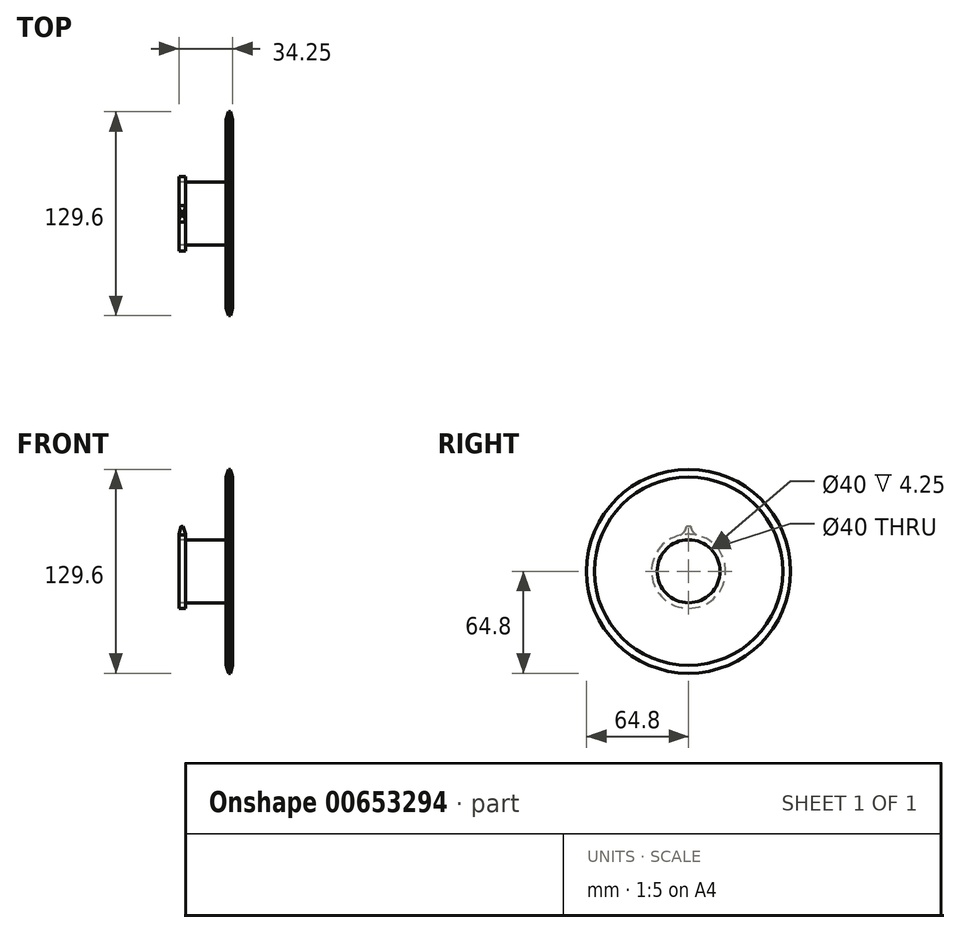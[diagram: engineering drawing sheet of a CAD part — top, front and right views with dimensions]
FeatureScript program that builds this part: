
annotation { "Feature Type Name" : "Feature", "Feature Type Description" : "" }
export const myFeature = defineFeature(function(context is Context, id is Id, definition is map)
    precondition{}
    {
        {
            var Q0;
            Q0=qCreatedBy(makeId("Front.planeOp"),FACE);
            var sketch = newSketch(context, id + "F0", { "sketchPlane" : qUnion([Q0])});
            skLineSegment(sketch, "E0", {"start": v(0, 20) * mm, "end": v(4.25, 20) * mm});
            skLineSegment(sketch, "E1", {"start": v(4.25, 20) * mm, "end": v(4.25, 28.55) * mm});
            skLineSegment(sketch, "E2", {"start": v(4.25, 28.55) * mm, "end": v(0, 28.55) * mm});
            skLineSegment(sketch, "E3", {"start": v(0, 28.55) * mm, "end": v(0, 20) * mm});
            skLineSegment(sketch, "E4", {"start": v(0, 0) * mm, "end": v(23.45, 0) * mm, "construction": true});
            skSolve(sketch);
        }
        {
            var Q0;
            Q0=makeQuery(id+"F0.imprint","IMPRINT",FACE,{"disambiguationData":[TD([[makeQuery(id+"F0.imprint","IMPRINT",EDGE,{"derivedFrom":sQuery(id+"F0.wireOp",EDGE,"E0")}),1.0]])]});
            var Q1;
            Q1=sQuery(id+"F0.wireOp",EDGE,"E4");
            revolve(context, id + "F1", {"entities" : qUnion([Q0]), "axis" : qUnion([Q1]), "revolveType" : RevolveType.FULL});
        }
        {
            var Q0;
            Q0=makeQuery(id+"F1.opRevolve","SWEPT_EDGE",EDGE,{"disambiguationData":[OSD([sQuery(id+"F0.wireOp",EDGE,"E1"),sQuery(id+"F0.wireOp",EDGE,"E2")])]});
            var Q1;
            Q1=makeQuery(id+"F1.opRevolve","SWEPT_EDGE",EDGE,{"disambiguationData":[OSD([sQuery(id+"F0.wireOp",EDGE,"E2"),sQuery(id+"F0.wireOp",EDGE,"E3")])]});
            chamfer(context, id + "F2", {"entities" : qUnion([Q0, Q1]), "chamferType" : ChamferType.TWO_OFFSETS, "width1" : 1.5 * mm, "oppositeDirection" : false, "width2" : 5 * mm});
        }
        {
            var Q0;
            Q0=makeQuery(id+"F1.opRevolve","SWEPT_FACE",FACE,{"disambiguationData":[OSD([sQuery(id+"F0.wireOp",EDGE,"E3")])]});
            var sketch = newSketch(context, id + "F3", { "sketchPlane" : qUnion([Q0])});
            skCircle(sketch, "E5.1", {"center": v(0, 0) * mm, "radius": 20 * mm});
            skLineSegment(sketch, "E6", {"start": v(0, 29.71) * mm, "end": v(-0.16, 29.47) * mm});
            skLineSegment(sketch, "E7", {"start": v(0, 29.71) * mm, "end": v(0.16, 29.47) * mm});
            skLineSegment(sketch, "E8", {"start": v(0, 0) * mm, "end": v(0, 29.47) * mm, "construction": true});
            skArc(sketch, "E9", {"start": v(-0.02, 29.47) * mm, "mid": v(0, 29.59) * mm, "end": v(0, 29.71) * mm});
            skArc(sketch, "E10.MirrorCS", {"start": v(0.02, 29.47) * mm, "mid": v(0, 29.59) * mm, "end": v(0, 29.71) * mm});
            skLineSegment(sketch, "E11", {"start": v(1.3, 29.47) * mm, "end": v(-1.3, 29.47) * mm});
            skArc(sketch, "E12", {"start": v(1.3, 29.47) * mm, "mid": v(2.4, 25.74) * mm, "end": v(5.14, 22.98) * mm});
            skArc(sketch, "E13.MirrorCS", {"start": v(-1.3, 29.47) * mm, "mid": v(-2.4, 25.74) * mm, "end": v(-5.14, 22.98) * mm});
            skPoint(sketch, "E14.orphan", {"position": v(4.22, 23.17) * mm});
            skLineSegment(sketch, "E15.trimOffspring", {"start": v(-0.16, 29.47) * mm, "end": v(0, 29.71) * mm});
            skPoint(sketch, "E16.trimOffspring.end.orphan", {"position": v(-4.22, 23.17) * mm});
            skArc(sketch, "E17.1.0", {"start": v(-13.96, 25.99) * mm, "mid": v(-13.32, 22.15) * mm, "end": v(-14.6, 18.47) * mm});
            skLineSegment(sketch, "E17.1.1", {"start": v(-11.62, 27.11) * mm, "end": v(-13.96, 25.99) * mm});
            skArc(sketch, "E17.1.2", {"start": v(-11.62, 27.11) * mm, "mid": v(-9, 24.23) * mm, "end": v(-5.34, 22.94) * mm});
            skArc(sketch, "E17.2.0", {"start": v(-23.85, 17.36) * mm, "mid": v(-21.61, 14.17) * mm, "end": v(-21.17, 10.3) * mm});
            skLineSegment(sketch, "E17.2.1", {"start": v(-22.23, 19.39) * mm, "end": v(-23.85, 17.36) * mm});
            skArc(sketch, "E17.2.2", {"start": v(-22.23, 19.39) * mm, "mid": v(-18.63, 17.92) * mm, "end": v(-14.76, 18.35) * mm});
            skArc(sketch, "E17.3.0", {"start": v(-29.02, 5.3) * mm, "mid": v(-25.62, 3.4) * mm, "end": v(-23.55, 0.1) * mm});
            skLineSegment(sketch, "E17.3.1", {"start": v(-28.44, 7.82) * mm, "end": v(-29.02, 5.3) * mm});
            skArc(sketch, "E17.3.2", {"start": v(-28.44, 7.82) * mm, "mid": v(-24.56, 8.06) * mm, "end": v(-21.26, 10.13) * mm});
            skArc(sketch, "E17.4.0", {"start": v(-28.44, -7.82) * mm, "mid": v(-24.56, -8.06) * mm, "end": v(-21.26, -10.13) * mm});
            skLineSegment(sketch, "E17.4.1", {"start": v(-29.02, -5.3) * mm, "end": v(-28.44, -7.82) * mm});
            skArc(sketch, "E17.4.2", {"start": v(-29.02, -5.3) * mm, "mid": v(-25.62, -3.4) * mm, "end": v(-23.55, -0.1) * mm});
            skArc(sketch, "E17.5.0", {"start": v(-22.23, -19.39) * mm, "mid": v(-18.63, -17.92) * mm, "end": v(-14.76, -18.35) * mm});
            skLineSegment(sketch, "E17.5.1", {"start": v(-23.85, -17.36) * mm, "end": v(-22.23, -19.39) * mm});
            skArc(sketch, "E17.5.2", {"start": v(-23.85, -17.36) * mm, "mid": v(-21.61, -14.17) * mm, "end": v(-21.17, -10.3) * mm});
            skArc(sketch, "E17.6.0", {"start": v(-11.62, -27.11) * mm, "mid": v(-9, -24.23) * mm, "end": v(-5.34, -22.94) * mm});
            skLineSegment(sketch, "E17.6.1", {"start": v(-13.96, -25.99) * mm, "end": v(-11.62, -27.11) * mm});
            skArc(sketch, "E17.6.2", {"start": v(-13.96, -25.99) * mm, "mid": v(-13.32, -22.15) * mm, "end": v(-14.6, -18.47) * mm});
            skArc(sketch, "E17.7.0", {"start": v(1.3, -29.47) * mm, "mid": v(2.4, -25.74) * mm, "end": v(5.14, -22.98) * mm});
            skLineSegment(sketch, "E17.7.1", {"start": v(-1.3, -29.47) * mm, "end": v(1.3, -29.47) * mm});
            skArc(sketch, "E17.7.2", {"start": v(-1.3, -29.47) * mm, "mid": v(-2.4, -25.74) * mm, "end": v(-5.14, -22.98) * mm});
            skArc(sketch, "E17.8.0", {"start": v(13.96, -25.99) * mm, "mid": v(13.32, -22.15) * mm, "end": v(14.6, -18.47) * mm});
            skLineSegment(sketch, "E17.8.1", {"start": v(11.62, -27.11) * mm, "end": v(13.96, -25.99) * mm});
            skArc(sketch, "E17.8.2", {"start": v(11.62, -27.11) * mm, "mid": v(9, -24.23) * mm, "end": v(5.34, -22.94) * mm});
            skArc(sketch, "E17.9.0", {"start": v(23.85, -17.36) * mm, "mid": v(21.61, -14.17) * mm, "end": v(21.17, -10.3) * mm});
            skLineSegment(sketch, "E17.9.1", {"start": v(22.23, -19.39) * mm, "end": v(23.85, -17.36) * mm});
            skArc(sketch, "E17.9.2", {"start": v(22.23, -19.39) * mm, "mid": v(18.63, -17.92) * mm, "end": v(14.76, -18.35) * mm});
            skArc(sketch, "E17.10.0", {"start": v(29.02, -5.3) * mm, "mid": v(25.62, -3.4) * mm, "end": v(23.55, -0.1) * mm});
            skLineSegment(sketch, "E17.10.1", {"start": v(28.44, -7.82) * mm, "end": v(29.02, -5.3) * mm});
            skArc(sketch, "E17.10.2", {"start": v(28.44, -7.82) * mm, "mid": v(24.56, -8.06) * mm, "end": v(21.26, -10.13) * mm});
            skArc(sketch, "E17.11.0", {"start": v(28.44, 7.82) * mm, "mid": v(24.56, 8.06) * mm, "end": v(21.26, 10.13) * mm});
            skLineSegment(sketch, "E17.11.1", {"start": v(29.02, 5.3) * mm, "end": v(28.44, 7.82) * mm});
            skArc(sketch, "E17.11.2", {"start": v(29.02, 5.3) * mm, "mid": v(25.62, 3.4) * mm, "end": v(23.55, 0.1) * mm});
            skArc(sketch, "E17.12.0", {"start": v(22.23, 19.39) * mm, "mid": v(18.63, 17.92) * mm, "end": v(14.76, 18.35) * mm});
            skLineSegment(sketch, "E17.12.1", {"start": v(23.85, 17.36) * mm, "end": v(22.23, 19.39) * mm});
            skArc(sketch, "E17.12.2", {"start": v(23.85, 17.36) * mm, "mid": v(21.61, 14.17) * mm, "end": v(21.17, 10.3) * mm});
            skArc(sketch, "E17.13.0", {"start": v(11.62, 27.11) * mm, "mid": v(9, 24.23) * mm, "end": v(5.34, 22.94) * mm});
            skLineSegment(sketch, "E17.13.1", {"start": v(13.96, 25.99) * mm, "end": v(11.62, 27.11) * mm});
            skArc(sketch, "E17.13.2", {"start": v(13.96, 25.99) * mm, "mid": v(13.32, 22.15) * mm, "end": v(14.6, 18.47) * mm});
            skSolve(sketch);
        }
        {
            var Q0;
            {var subQ5=sQuery(id+"F3.wireOp",EDGE,"E12");Q0=makeQuery(id+"F3.imprint","IMPRINT",FACE,{"disambiguationData":[TD([[makeQuery(id+"F3.imprint","IMPRINT",EDGE,{"derivedFrom":subQ5}),-1.0]])]});}
            var Q1;
            Q1=makeQuery(id+"F3.imprint","IMPRINT",FACE,{"disambiguationData":[TD([[makeQuery(id+"F3.imprint","IMPRINT",EDGE,{"derivedFrom":sQuery(id+"F3.wireOp",EDGE,"E5.1")}),-1.0]])]});
            var Q2;
            {var subQ0=sQuery(id+"F3.wireOp",EDGE,"E17.13.0");Q2=makeQuery(id+"F3.imprint","IMPRINT",FACE,{"disambiguationData":[TD([[makeQuery(id+"F3.imprint","IMPRINT",EDGE,{"derivedFrom":subQ0}),1.0]])]});}
            var Q3;
            {var subQ0=sQuery(id+"F3.wireOp",EDGE,"E17.12.0");Q3=makeQuery(id+"F3.imprint","IMPRINT",FACE,{"disambiguationData":[TD([[makeQuery(id+"F3.imprint","IMPRINT",EDGE,{"derivedFrom":subQ0}),1.0]])]});}
            var Q4;
            {var subQ0=sQuery(id+"F3.wireOp",EDGE,"E17.11.0");Q4=makeQuery(id+"F3.imprint","IMPRINT",FACE,{"disambiguationData":[TD([[makeQuery(id+"F3.imprint","IMPRINT",EDGE,{"derivedFrom":subQ0}),1.0]])]});}
            var Q5;
            {var subQ0=sQuery(id+"F3.wireOp",EDGE,"E17.10.0");Q5=makeQuery(id+"F3.imprint","IMPRINT",FACE,{"disambiguationData":[TD([[makeQuery(id+"F3.imprint","IMPRINT",EDGE,{"derivedFrom":subQ0}),1.0]])]});}
            var Q6;
            {var subQ0=sQuery(id+"F3.wireOp",EDGE,"E17.9.0");Q6=makeQuery(id+"F3.imprint","IMPRINT",FACE,{"disambiguationData":[TD([[makeQuery(id+"F3.imprint","IMPRINT",EDGE,{"derivedFrom":subQ0}),1.0]])]});}
            var Q7;
            {var subQ0=sQuery(id+"F3.wireOp",EDGE,"E17.8.0");Q7=makeQuery(id+"F3.imprint","IMPRINT",FACE,{"disambiguationData":[TD([[makeQuery(id+"F3.imprint","IMPRINT",EDGE,{"derivedFrom":subQ0}),1.0]])]});}
            var Q8;
            {var subQ0=sQuery(id+"F3.wireOp",EDGE,"E17.7.0");Q8=makeQuery(id+"F3.imprint","IMPRINT",FACE,{"disambiguationData":[TD([[makeQuery(id+"F3.imprint","IMPRINT",EDGE,{"derivedFrom":subQ0}),1.0]])]});}
            var Q9;
            {var subQ0=sQuery(id+"F3.wireOp",EDGE,"E17.6.0");Q9=makeQuery(id+"F3.imprint","IMPRINT",FACE,{"disambiguationData":[TD([[makeQuery(id+"F3.imprint","IMPRINT",EDGE,{"derivedFrom":subQ0}),1.0]])]});}
            var Q10;
            {var subQ0=sQuery(id+"F3.wireOp",EDGE,"E17.5.0");Q10=makeQuery(id+"F3.imprint","IMPRINT",FACE,{"disambiguationData":[TD([[makeQuery(id+"F3.imprint","IMPRINT",EDGE,{"derivedFrom":subQ0}),1.0]])]});}
            var Q11;
            {var subQ0=sQuery(id+"F3.wireOp",EDGE,"E17.4.0");Q11=makeQuery(id+"F3.imprint","IMPRINT",FACE,{"disambiguationData":[TD([[makeQuery(id+"F3.imprint","IMPRINT",EDGE,{"derivedFrom":subQ0}),1.0]])]});}
            var Q12;
            {var subQ0=sQuery(id+"F3.wireOp",EDGE,"E17.3.0");Q12=makeQuery(id+"F3.imprint","IMPRINT",FACE,{"disambiguationData":[TD([[makeQuery(id+"F3.imprint","IMPRINT",EDGE,{"derivedFrom":subQ0}),1.0]])]});}
            var Q13;
            {var subQ0=sQuery(id+"F3.wireOp",EDGE,"E17.2.0");Q13=makeQuery(id+"F3.imprint","IMPRINT",FACE,{"disambiguationData":[TD([[makeQuery(id+"F3.imprint","IMPRINT",EDGE,{"derivedFrom":subQ0}),1.0]])]});}
            var Q14;
            {var subQ0=sQuery(id+"F3.wireOp",EDGE,"E17.1.0");Q14=makeQuery(id+"F3.imprint","IMPRINT",FACE,{"disambiguationData":[TD([[makeQuery(id+"F3.imprint","IMPRINT",EDGE,{"derivedFrom":subQ0}),1.0]])]});}
            extrude(context, id + "F4", {"entities" : qUnion([Q0, Q1, Q2, Q3, Q4, Q5, Q6, Q7, Q8, Q9, Q10, Q11, Q12, Q13, Q14]), "operationType" : NewBodyOperationType.INTERSECT, "oppositeDirection" : true, "depth" : 25 * mm, "offsetDistance" : 25 * mm});
        }
        {
            var Q0;
            Q0=qCreatedBy(makeId("Front.planeOp"),FACE);
            var sketch = newSketch(context, id + "F5", { "sketchPlane" : qUnion([Q0])});
            skPoint(sketch, "E18.0", {"position": v(2.13, 0.1) * mm});
            skLineSegment(sketch, "E19", {"start": v(2.13, 0) * mm, "end": v(32.12, 0) * mm, "construction": true});
            skLineSegment(sketch, "E20", {"start": v(30, 20) * mm, "end": v(34.25, 20) * mm});
            skLineSegment(sketch, "E21", {"start": v(34.25, 20) * mm, "end": v(34.25, 64.8) * mm});
            skLineSegment(sketch, "E22", {"start": v(34.25, 64.8) * mm, "end": v(30, 64.8) * mm});
            skLineSegment(sketch, "E23", {"start": v(30, 64.8) * mm, "end": v(30, 20) * mm});
            skLineSegment(sketch, "E24", {"start": v(30, 0) * mm, "end": v(53.45, 0) * mm, "construction": true});
            skSolve(sketch);
        }
        {
            var Q0;
            Q0=makeQuery(id+"F5.imprint","IMPRINT",FACE,{"disambiguationData":[TD([[makeQuery(id+"F5.imprint","IMPRINT",EDGE,{"derivedFrom":sQuery(id+"F5.wireOp",EDGE,"E20")}),1.0]])]});
            var Q1;
            Q1=sQuery(id+"F5.wireOp",EDGE,"E24");
            revolve(context, id + "F6", {"entities" : qUnion([Q0]), "axis" : qUnion([Q1]), "revolveType" : RevolveType.FULL});
        }
        {
            var Q0;
            Q0=makeQuery(id+"F6.opRevolve","SWEPT_EDGE",EDGE,{"disambiguationData":[OSD([sQuery(id+"F5.wireOp",EDGE,"E21"),sQuery(id+"F5.wireOp",EDGE,"E22")])]});
            var Q1;
            Q1=makeQuery(id+"F6.opRevolve","SWEPT_EDGE",EDGE,{"disambiguationData":[OSD([sQuery(id+"F5.wireOp",EDGE,"E22"),sQuery(id+"F5.wireOp",EDGE,"E23")])]});
            chamfer(context, id + "F7", {"entities" : qUnion([Q0, Q1]), "chamferType" : ChamferType.TWO_OFFSETS, "width1" : 1.5 * mm, "oppositeDirection" : false, "width2" : 5 * mm, "tangentPropagation" : true});
        }
        {
            var Q0;
            Q0=makeQuery(id+"F6.opRevolve","SWEPT_FACE",FACE,{"disambiguationData":[OSD([sQuery(id+"F5.wireOp",EDGE,"E23")])]});
            var sketch = newSketch(context, id + "F8", { "sketchPlane" : qUnion([Q0])});
            skCircle(sketch, "E25.1", {"center": v(0, 0) * mm, "radius": 20 * mm});
            skLineSegment(sketch, "E26", {"start": v(0, 29.71) * mm, "end": v(-0.16, 29.47) * mm});
            skLineSegment(sketch, "E27", {"start": v(0, 29.71) * mm, "end": v(0.16, 29.47) * mm});
            skLineSegment(sketch, "E28", {"start": v(0, 0) * mm, "end": v(0, 29.47) * mm, "construction": true});
            skArc(sketch, "E29", {"start": v(-0.02, 29.47) * mm, "mid": v(0, 29.59) * mm, "end": v(0, 29.71) * mm});
            skArc(sketch, "E30.MirrorCS", {"start": v(0.02, 29.47) * mm, "mid": v(0, 29.59) * mm, "end": v(0, 29.71) * mm});
            skLineSegment(sketch, "E31", {"start": v(1.3, 29.47) * mm, "end": v(-1.3, 29.47) * mm});
            skArc(sketch, "E32", {"start": v(1.3, 29.47) * mm, "mid": v(2.4, 25.74) * mm, "end": v(5.14, 22.98) * mm});
            skArc(sketch, "E33.MirrorCS", {"start": v(-1.3, 29.47) * mm, "mid": v(-2.4, 25.74) * mm, "end": v(-5.14, 22.98) * mm});
            skPoint(sketch, "E34.orphan", {"position": v(4.22, 23.17) * mm});
            skLineSegment(sketch, "E35.trimOffspring", {"start": v(-0.16, 29.47) * mm, "end": v(0, 29.71) * mm});
            skPoint(sketch, "E36.trimOffspring.end.orphan", {"position": v(-4.22, 23.17) * mm});
            skArc(sketch, "E37.1.0", {"start": v(-13.96, 25.99) * mm, "mid": v(-13.32, 22.15) * mm, "end": v(-14.6, 18.47) * mm});
            skLineSegment(sketch, "E37.1.1", {"start": v(-11.62, 27.11) * mm, "end": v(-13.96, 25.99) * mm});
            skArc(sketch, "E37.1.2", {"start": v(-11.62, 27.11) * mm, "mid": v(-9, 24.23) * mm, "end": v(-5.34, 22.94) * mm});
            skArc(sketch, "E37.2.0", {"start": v(-23.85, 17.36) * mm, "mid": v(-21.61, 14.17) * mm, "end": v(-21.17, 10.3) * mm});
            skLineSegment(sketch, "E37.2.1", {"start": v(-22.23, 19.39) * mm, "end": v(-23.85, 17.36) * mm});
            skArc(sketch, "E37.2.2", {"start": v(-22.23, 19.39) * mm, "mid": v(-18.63, 17.92) * mm, "end": v(-14.76, 18.35) * mm});
            skArc(sketch, "E37.3.0", {"start": v(-29.02, 5.3) * mm, "mid": v(-25.62, 3.4) * mm, "end": v(-23.55, 0.1) * mm});
            skLineSegment(sketch, "E37.3.1", {"start": v(-28.44, 7.82) * mm, "end": v(-29.02, 5.3) * mm});
            skArc(sketch, "E37.3.2", {"start": v(-28.44, 7.82) * mm, "mid": v(-24.56, 8.06) * mm, "end": v(-21.26, 10.13) * mm});
            skArc(sketch, "E37.4.0", {"start": v(-28.44, -7.82) * mm, "mid": v(-24.56, -8.06) * mm, "end": v(-21.26, -10.13) * mm});
            skLineSegment(sketch, "E37.4.1", {"start": v(-29.02, -5.3) * mm, "end": v(-28.44, -7.82) * mm});
            skArc(sketch, "E37.4.2", {"start": v(-29.02, -5.3) * mm, "mid": v(-25.62, -3.4) * mm, "end": v(-23.55, -0.1) * mm});
            skArc(sketch, "E37.5.0", {"start": v(-22.23, -19.39) * mm, "mid": v(-18.63, -17.92) * mm, "end": v(-14.76, -18.35) * mm});
            skLineSegment(sketch, "E37.5.1", {"start": v(-23.85, -17.36) * mm, "end": v(-22.23, -19.39) * mm});
            skArc(sketch, "E37.5.2", {"start": v(-23.85, -17.36) * mm, "mid": v(-21.61, -14.17) * mm, "end": v(-21.17, -10.3) * mm});
            skArc(sketch, "E37.6.0", {"start": v(-11.62, -27.11) * mm, "mid": v(-9, -24.23) * mm, "end": v(-5.34, -22.94) * mm});
            skLineSegment(sketch, "E37.6.1", {"start": v(-13.96, -25.99) * mm, "end": v(-11.62, -27.11) * mm});
            skArc(sketch, "E37.6.2", {"start": v(-13.96, -25.99) * mm, "mid": v(-13.32, -22.15) * mm, "end": v(-14.6, -18.47) * mm});
            skArc(sketch, "E37.7.0", {"start": v(1.3, -29.47) * mm, "mid": v(2.4, -25.74) * mm, "end": v(5.14, -22.98) * mm});
            skLineSegment(sketch, "E37.7.1", {"start": v(-1.3, -29.47) * mm, "end": v(1.3, -29.47) * mm});
            skArc(sketch, "E37.7.2", {"start": v(-1.3, -29.47) * mm, "mid": v(-2.4, -25.74) * mm, "end": v(-5.14, -22.98) * mm});
            skArc(sketch, "E37.8.0", {"start": v(13.96, -25.99) * mm, "mid": v(13.32, -22.15) * mm, "end": v(14.6, -18.47) * mm});
            skLineSegment(sketch, "E37.8.1", {"start": v(11.62, -27.11) * mm, "end": v(13.96, -25.99) * mm});
            skArc(sketch, "E37.8.2", {"start": v(11.62, -27.11) * mm, "mid": v(9, -24.23) * mm, "end": v(5.34, -22.94) * mm});
            skArc(sketch, "E37.9.0", {"start": v(23.85, -17.36) * mm, "mid": v(21.61, -14.17) * mm, "end": v(21.17, -10.3) * mm});
            skLineSegment(sketch, "E37.9.1", {"start": v(22.23, -19.39) * mm, "end": v(23.85, -17.36) * mm});
            skArc(sketch, "E37.9.2", {"start": v(22.23, -19.39) * mm, "mid": v(18.63, -17.92) * mm, "end": v(14.76, -18.35) * mm});
            skArc(sketch, "E37.10.0", {"start": v(29.02, -5.3) * mm, "mid": v(25.62, -3.4) * mm, "end": v(23.55, -0.1) * mm});
            skLineSegment(sketch, "E37.10.1", {"start": v(28.44, -7.82) * mm, "end": v(29.02, -5.3) * mm});
            skArc(sketch, "E37.10.2", {"start": v(28.44, -7.82) * mm, "mid": v(24.56, -8.06) * mm, "end": v(21.26, -10.13) * mm});
            skArc(sketch, "E37.11.0", {"start": v(28.44, 7.82) * mm, "mid": v(24.56, 8.06) * mm, "end": v(21.26, 10.13) * mm});
            skLineSegment(sketch, "E37.11.1", {"start": v(29.02, 5.3) * mm, "end": v(28.44, 7.82) * mm});
            skArc(sketch, "E37.11.2", {"start": v(29.02, 5.3) * mm, "mid": v(25.62, 3.4) * mm, "end": v(23.55, 0.1) * mm});
            skArc(sketch, "E37.12.0", {"start": v(22.23, 19.39) * mm, "mid": v(18.63, 17.92) * mm, "end": v(14.76, 18.35) * mm});
            skLineSegment(sketch, "E37.12.1", {"start": v(23.85, 17.36) * mm, "end": v(22.23, 19.39) * mm});
            skArc(sketch, "E37.12.2", {"start": v(23.85, 17.36) * mm, "mid": v(21.61, 14.17) * mm, "end": v(21.17, 10.3) * mm});
            skArc(sketch, "E37.13.0", {"start": v(11.62, 27.11) * mm, "mid": v(9, 24.23) * mm, "end": v(5.34, 22.94) * mm});
            skLineSegment(sketch, "E37.13.1", {"start": v(13.96, 25.99) * mm, "end": v(11.62, 27.11) * mm});
            skArc(sketch, "E37.13.2", {"start": v(13.96, 25.99) * mm, "mid": v(13.32, 22.15) * mm, "end": v(14.6, 18.47) * mm});
            skSolve(sketch);
        }
        {
            var Q0;
            Q0=makeQuery(id+"F8.imprint","IMPRINT",FACE,{"disambiguationData":[TD([[makeQuery(id+"F8.imprint","IMPRINT",EDGE,{"derivedFrom":sQuery(id+"F8.wireOp",EDGE,"E25.1")}),-1.0]])]});
            var sketch = newSketch(context, id + "F9", { "sketchPlane" : qUnion([Q0])});
            skCircle(sketch, "E38.0", {"center": v(0, 0) * mm, "radius": 20 * mm});
            skSolve(sketch);
        }
        {
            var Q0;
            Q0 = qSketchRegion(id + "F9", true);
            var Q1;
            Q1=makeQuery(id+"F3.imprint","IMPRINT",FACE,{"disambiguationData":[TD([[makeQuery(id+"F3.imprint","IMPRINT",EDGE,{"derivedFrom":sQuery(id+"F3.wireOp",EDGE,"E5.1")}),1.0]])]});
            var Q2;
            Q2=makeQuery(id+"F6.opRevolve","SWEPT_FACE",FACE,{"disambiguationData":[OSD([sQuery(id+"F5.wireOp",EDGE,"E21")])]});
            extrude(context, id + "F10", {"entities" : qUnion([Q0, Q1]), "endBound" : BoundingType.UP_TO_SURFACE, "oppositeDirection" : true, "depth" : 25 * mm, "endBoundEntityFace" : qUnion([Q2]), "offsetDistance" : 25 * mm});
        }
        {
            var Q0;
            Q0=makeQuery(id+"F10.opExtrude","SWEPT_BODY",BODY,{"disambiguationData":[OSD([sQuery(id+"F9.wireOp",EDGE,"E38.0")])]});
            deleteBodies(context, id + "F11", {"entities" : qUnion([Q0])});
        }
    });
